# Revit family: STS-576_RV17_LOD400_(06.11.23)
name_source: partatom
category: Электрооборудование
revit_build: Autodesk Revit 2017 (Build: 20170118_1100(x64)
units: mm (PartAtom-declared; Revit-internal decimal feet)

## family parameters
Всегда вертикально = Нет
Конфигурация панели = Два столбца, слева направо
На основе рабочей плоскости = Нет
Общий = Нет
При загрузке вырезать с полостями = Нет
Размер круглого соединителя = Использовать диаметр
Тип детали = Щит
Точка расчета площади = Нет

## types (1)
- STS-576
    ADSK_URL страницы изделия = https://stilsoft.ru
    ADSK_Единица измерения = шт.
    ADSK_Завод-изготовитель = ООО «Основа Безопасности»
    ADSK_Количество = 1
    ADSK_Марка = СТВФ.426471.140
    ADSK_Масса = 2
    ADSK_Наименование = Блок связи станционный STS-576
    ADSK_Размер_Высота = 44 мм
    ADSK_Размер_Глубина = 208 мм
    ADSK_Размер_Длина = 490 мм
    d_короба = 20 мм
    Время непрерывной работы, ч = круглосуточно
    Диапазон рабочих температур, С = от –40 до +50
    Длина волны, нм = 1310
    Защита от переполюсовки = да
    Количество разъемов  RG-45, шт. = 8
    Количество разъемов SFP, шт. = 2
    Количество разъемов клеммная колодка, шт. = 1
    Напряжение = 12
    Напряжение электропитания переменного тока, В/ Гц = 220 / 50
    Напряжение электропитания постоянного тока, В = 12 ± 10%
    Поддерживаемые стандарты Ethеrnеt = EEE802.3u 100BASE-TX, IEEE802.3 10BASE-T, IEEE802.3z 1000Base-X, IEEE802.3x Flow Control
    Потребляемый ток при напряжении 12В, не более, А = 4 А
    Потребляемый ток при напряжении 220В, не более, А = 1 А
    Расстояние передачи данных (информации), дальность действия по кабелю UTP-5e, до, м = 100 мм
    Расстояние передачи данных (информации), дальность действия по оптическому кабелю, до, м = 20000 мм
    Скорость передачи данных Ethernet (RG-45), Мбит/с = 10/100/1000
    Скорость передачи данных SFP (оптический порт), Мбит/с = 10/100/1000
    Тип кабеля = SМ 9/125 μm
    Тип разъема = 2xLC
